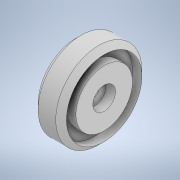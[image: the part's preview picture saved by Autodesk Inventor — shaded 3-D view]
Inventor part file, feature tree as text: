
AUTODESK INVENTOR PART (.ipt)
format: ipt  version: 2022 (Build 260153000, 153)  size: 156,672 bytes
history: native  units: mm
features: sketch x4, revolve x2, other x1, extrude x1, hole x1
ambient origin geometry x8: Origin, YZ Plane, XZ Plane, XY Plane, X Axis, Y Axis, Z Axis, Center Point
bodies: Body1 (feature_tree)
feature tree (9):
  other  "Твердое тело1"
  revolve  "Вращение1"
  revolve  "Вращение2"
  extrude  "Выдавливание1"  Depth=20.0mm
  hole  "Отверстие1"  [1 undecoded]
  sketch  "Эскиз1"
  sketch  "Эскиз2"
  sketch  "Эскиз3"
  sketch  "Эскиз4"
note: 1 required parameter value undecoded (feature->parameter linkage not recoverable at this tier; creation-order binding heuristic only, values carry confidence <= 0.55)
